# Revit family: GRAS_HZ-4
name_source: partatom
category: Osprzęt hydrauliczny
revit_build: Autodesk Revit 2018 (Build: 20190510_1515(x64)
units: mm (PartAtom-declared; Revit-internal decimal feet)

## family parameters
Obiekt nadrzędny = Powierzchnia
Punkt obliczania pomieszczeń = Nie
Tnij formami wycięć po wczytaniu = Nie
Typ części = Normalny
Współdzielony = Nie
Wymiar okrągłego złącza = Użyj średnicy

## types (1)
- HZ-4, RAL3000
    0 = 0 mm  [stored 0 ft]
    Base_Height = 230 mm  [stored 0.754593 ft]
    Cabinet depth = 500 mm  [stored 1.64042 ft]
    Cabinet height = 1250 mm  [stored 4.10105 ft]
    Cabinet material = DC01, RAL3000
    Cabinet width = 700 mm  [stored 2.29659 ft]
    Domyślna rzędna = 0 mm  [stored 0 ft]
    Model = HZ-4, RAL3000
    Opis = https://gras.pl
    Producent = GRAS PPPH
    URL = http://www.gras.pl

note: [stored X ft] marks values corroborated as IEEE doubles in the binary element streams (Revit-internal decimal feet)

## geometry (parser evidence)
native form markers: Blend x8
no freeform markers — native parametric forms only
